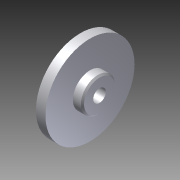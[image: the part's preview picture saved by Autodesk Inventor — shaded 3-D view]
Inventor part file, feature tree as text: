
AUTODESK INVENTOR PART (.ipt)
format: ipt  version: 2012 (Build 160160000, 160)  size: 640,512 bytes
history: native  units: in
note: dims shown in document units (in); Inventor stores cm internally (conversion verified against a paired STEP export)
features: extrude x3, sketch x1, chamfer x1, imported_body x1
ambient origin geometry x8: Origin, YZ Plane, XZ Plane, XY Plane, X Axis, Y Axis, Z Axis, Center Point
feature tree (6):
  sketch  "Sketch1"  dims[d0=0.25in d1=0.5625in d2=0.0in d3=1.75in d4=1.0in d5=0.0in d9=0.1875in d10=0.0in d11=0.0312in d12=0.125in d13=45.0deg]
  extrude  "Extrusion1"  Depth=0.5625in TaperAngle=0.0deg
  extrude  "Extrusion2"  Depth=1.75in
  extrude  "Extrusion4"  Depth=1.0in TaperAngle=0.0deg
  chamfer  "Chamfer1"  Distance=0.1875in
  imported_body  "Base1"
